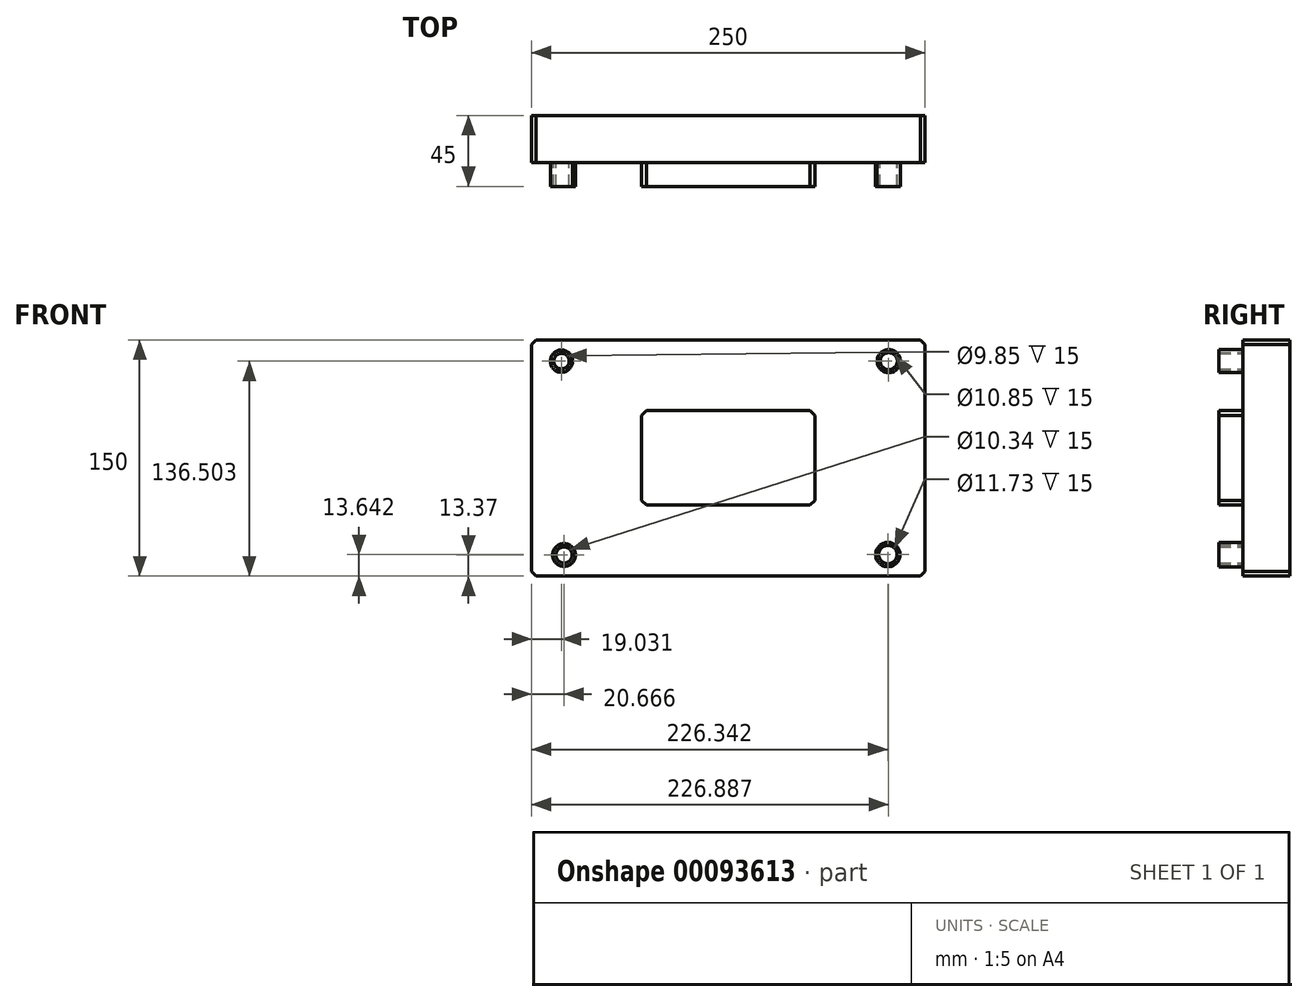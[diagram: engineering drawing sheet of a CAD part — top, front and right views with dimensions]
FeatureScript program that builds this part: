
annotation { "Feature Type Name" : "Feature", "Feature Type Description" : "" }
export const myFeature = defineFeature(function(context is Context, id is Id, definition is map)
    precondition{}
    {
        {
            var Q0;
            Q0=qCreatedBy(makeId("Front.planeOp"),FACE);
            var sketch = newSketch(context, id + "F0", { "sketchPlane" : qUnion([Q0])});
            skLineSegment(sketch, "E0", {"start": v(-114.03, 92.18) * mm, "end": v(135.97, 92.18) * mm});
            skLineSegment(sketch, "E1", {"start": v(-114.03, 92.18) * mm, "end": v(-114.03, -57.82) * mm});
            skLineSegment(sketch, "E2", {"start": v(-114.03, -57.82) * mm, "end": v(135.97, -57.82) * mm});
            skLineSegment(sketch, "E3", {"start": v(135.97, -57.82) * mm, "end": v(135.97, 92.18) * mm});
            skSolve(sketch);
        }
        {
            var Q0;
            Q0=makeQuery(id+"F0.imprint","IMPRINT",FACE,{"disambiguationData":[TD([[makeQuery(id+"F0.imprint","IMPRINT",EDGE,{"derivedFrom":sQuery(id+"F0.wireOp",EDGE,"E0")}),-1.0]])]});
            extrude(context, id + "F1", {"entities" : qUnion([Q0]), "depth" : 30 * mm});
        }
        {
            var Q0;
            Q0=makeQuery(id+"F1.opExtrude","SWEPT_EDGE",EDGE,{"disambiguationData":[OSD([sQuery(id+"F0.wireOp",EDGE,"E1"),sQuery(id+"F0.wireOp",EDGE,"E2")])]});
            chamfer(context, id + "F2", {"entities" : qUnion([Q0]), "width" : 3 * mm, "tangentPropagation" : true});
        }
        {
            var Q0;
            Q0=makeQuery(id+"F1.opExtrude","SWEPT_EDGE",EDGE,{"disambiguationData":[OSD([sQuery(id+"F0.wireOp",EDGE,"E2"),sQuery(id+"F0.wireOp",EDGE,"E3")])]});
            chamfer(context, id + "F3", {"entities" : qUnion([Q0]), "width" : 3 * mm, "tangentPropagation" : true});
        }
        {
            var Q0;
            Q0=makeQuery(id+"F1.opExtrude","SWEPT_EDGE",EDGE,{"disambiguationData":[OSD([sQuery(id+"F0.wireOp",EDGE,"E0"),sQuery(id+"F0.wireOp",EDGE,"E3")])]});
            chamfer(context, id + "F4", {"entities" : qUnion([Q0]), "width" : 3 * mm, "tangentPropagation" : true});
        }
        {
            var Q0;
            Q0=makeQuery(id+"F1.opExtrude","SWEPT_EDGE",EDGE,{"disambiguationData":[OSD([sQuery(id+"F0.wireOp",EDGE,"E0"),sQuery(id+"F0.wireOp",EDGE,"E1")])]});
            chamfer(context, id + "F5", {"entities" : qUnion([Q0]), "width" : 3 * mm, "tangentPropagation" : true});
        }
        {
            var Q0;
            Q0=makeQuery(id+"F1.opExtrude","CAP_FACE",FACE,{"disambiguationData":[OSD([sQuery(id+"F0.wireOp",EDGE,"E0"),sQuery(id+"F0.wireOp",EDGE,"E1"),sQuery(id+"F0.wireOp",EDGE,"E2"),sQuery(id+"F0.wireOp",EDGE,"E3")])],"isStart":false});
            var sketch = newSketch(context, id + "F6", { "sketchPlane" : qUnion([Q0])});
            skPoint(sketch, "E4.endSnap0", {"position": v(10.97, 92.18) * mm});
            skLineSegment(sketch, "E5", {"start": v(-44.03, 47.18) * mm, "end": v(-44.03, -12.82) * mm});
            skLineSegment(sketch, "E6", {"start": v(-44.03, -12.82) * mm, "end": v(65.97, -12.82) * mm});
            skLineSegment(sketch, "E7", {"start": v(65.97, -12.82) * mm, "end": v(65.97, 47.18) * mm});
            skLineSegment(sketch, "E8", {"start": v(-44.03, 47.18) * mm, "end": v(65.97, 47.18) * mm});
            skSolve(sketch);
        }
        {
            var Q0;
            Q0=makeQuery(id+"F6.imprint","IMPRINT",FACE,{"disambiguationData":[TD([[makeQuery(id+"F6.imprint","IMPRINT",EDGE,{"derivedFrom":sQuery(id+"F6.wireOp",EDGE,"E5")}),1.0]])]});
            extrude(context, id + "F7", {"entities" : qUnion([Q0]), "operationType" : NewBodyOperationType.ADD, "depth" : 15 * mm});
        }
        {
            var Q0;
            Q0=makeQuery(id+"F7.opExtrude","SWEPT_EDGE",EDGE,{"disambiguationData":[OSD([sQuery(id+"F6.wireOp",EDGE,"E5"),sQuery(id+"F6.wireOp",EDGE,"E6")])]});
            var Q1;
            Q1=makeQuery(id+"F7.opExtrude","SWEPT_EDGE",EDGE,{"disambiguationData":[OSD([sQuery(id+"F6.wireOp",EDGE,"E5"),sQuery(id+"F6.wireOp",EDGE,"E8")])]});
            var Q2;
            Q2=makeQuery(id+"F7.opExtrude","SWEPT_EDGE",EDGE,{"disambiguationData":[OSD([sQuery(id+"F6.wireOp",EDGE,"E6"),sQuery(id+"F6.wireOp",EDGE,"E7")])]});
            var Q3;
            Q3=makeQuery(id+"F7.opExtrude","SWEPT_EDGE",EDGE,{"disambiguationData":[OSD([sQuery(id+"F6.wireOp",EDGE,"E7"),sQuery(id+"F6.wireOp",EDGE,"E8")])]});
            chamfer(context, id + "F8", {"entities" : qUnion([Q0, Q1, Q2, Q3]), "width" : 3 * mm, "tangentPropagation" : true});
        }
        {
            var Q0;
            Q0=makeQuery(id+"F1.opExtrude","CAP_FACE",FACE,{"disambiguationData":[OSD([sQuery(id+"F0.wireOp",EDGE,"E0"),sQuery(id+"F0.wireOp",EDGE,"E1"),sQuery(id+"F0.wireOp",EDGE,"E2"),sQuery(id+"F0.wireOp",EDGE,"E3")])],"isStart":false});
            var sketch = newSketch(context, id + "F9", { "sketchPlane" : qUnion([Q0])});
            skCircle(sketch, "E9", {"center": v(-95, 78.68) * mm, "radius": 4.93 * mm});
            skCircle(sketch, "E10", {"center": v(-95, 78.68) * mm, "radius": 7.07 * mm});
            skCircle(sketch, "E11", {"center": v(112.86, 78.68) * mm, "radius": 7.34 * mm});
            skCircle(sketch, "E12", {"center": v(112.86, 78.68) * mm, "radius": 5.43 * mm});
            skCircle(sketch, "E13", {"center": v(-93.36, -44.45) * mm, "radius": 7.22 * mm});
            skCircle(sketch, "E14", {"center": v(-93.36, -44.45) * mm, "radius": 5.17 * mm});
            skCircle(sketch, "E15", {"center": v(112.31, -44.18) * mm, "radius": 7.75 * mm});
            skCircle(sketch, "E16", {"center": v(112.31, -44.18) * mm, "radius": 5.86 * mm});
            skSolve(sketch);
        }
        {
            var Q0;
            Q0=makeQuery(id+"F9.imprint","IMPRINT",FACE,{"disambiguationData":[TD([[makeQuery(id+"F9.imprint","IMPRINT",EDGE,{"derivedFrom":sQuery(id+"F9.wireOp",EDGE,"E13")}),1.0]])]});
            var Q1;
            Q1=makeQuery(id+"F9.imprint","IMPRINT",FACE,{"disambiguationData":[TD([[makeQuery(id+"F9.imprint","IMPRINT",EDGE,{"derivedFrom":sQuery(id+"F9.wireOp",EDGE,"E15")}),1.0]])]});
            var Q2;
            Q2=makeQuery(id+"F9.imprint","IMPRINT",FACE,{"disambiguationData":[TD([[makeQuery(id+"F9.imprint","IMPRINT",EDGE,{"derivedFrom":sQuery(id+"F9.wireOp",EDGE,"E11")}),1.0]])]});
            var Q3;
            Q3=makeQuery(id+"F9.imprint","IMPRINT",FACE,{"disambiguationData":[TD([[makeQuery(id+"F9.imprint","IMPRINT",EDGE,{"derivedFrom":sQuery(id+"F9.wireOp",EDGE,"E9")}),-1.0]])]});
            extrude(context, id + "F10", {"entities" : qUnion([Q0, Q1, Q2, Q3]), "operationType" : NewBodyOperationType.ADD, "depth" : 15 * mm});
        }
    });
